# Revit family: Rohrschelle Titan HD, M12, Silikon
name_source: partatom
category: HLS-Bauteile
revit_build: Autodesk Revit 2017 (Build: 20190507_1515(x64)
units: mm (PartAtom-declared; Revit-internal decimal feet)

## family parameters
Arbeitsebenenbasiert = Ja
Beim Laden mit Abzugskörper schneiden = Nein
Bemaßung runder Anschluss = Durchmesser verwenden
Gemeinsam genutzt = Ja
Immer vertikal = Nein
Raumberechnungspunkt = Nein
Teiletyp = Normal

## types (30) — shared parameters
A = 22 mm  [stored 0.0721785 ft]
Anschluss = M12
Anschlußhöhe = 22 mm
Bauart = zweiteilig
Baustoffklasse = B2
Brandschutz = RAL GZ 656
DF1 = 29 mm  [stored 0.0951444 ft]
DS = 6 mm  [stored 0.019685 ft]
DVS = 13 mm
Dämmstärke = 6 mm  [stored 0.019685 ft]
Fabrikat = MEFA
Farbe Schalldämmeinlage = rot
Firma = MEFA Befestigungs- und Montagesysteme GmbH
HGA = 11 mm  [stored 0.0360892 ft]
Kurztext1 = Rohrschelle Titan HD 50x5,0
MB = 50 mm  [stored 0.164042 ft]
MD = 5 mm  [stored 0.0164042 ft]
Material = Stahl
Material Schalldämmeinlage = Silikon
Materialmaße = 50x5,0 mm
Materialname = S235
Mengeneinheit = St
Oberflaeche = galvanisch verzinkt
Schalldämmeinlage = Silikon
Verschluss = Schraubverschluss
Verschluss-Schraube = M12
Vorgabe-Ansicht = 1219 mm
max. Temperaturbeständigkeit = 250 °C
max. zul. Last horizontal = 0.00 kN
max. zul. Last vertikal = 0.00 kN
vpe = 1 St
zero-valued in all types: Nennweite DN Rohr, Stärke Material, max. Rohraußendurchmesser, min. Rohraußendurchmesser

## per-type parameters (varying)
| type | Achsabstand | Artikelnummer | B | Breite | D | D0 | DF2 | EAN | Gewicht | Gewicht pro Bauteil | H | Höhe | Kurztext2 | R | RM | Rohraußendurchmesser | Rohraußendurchmesser Zoll | S | max. Höhe | max. zul. Last |
| Titan HD, M12, Ø 64, Silikon | 125 mm | 0067500 | 154 mm | 154 mm | 64 mm  [stored 0.209974 ft] | 76 mm  [stored 0.249344 ft] | 19 mm  [stored 0.062336 ft] | 4250928402059 | 0.92 kg | 0.92 kg | 97 mm | 97 mm | 64 mm M12 Silikon | 38 mm  [stored 0.124672 ft] | 43 mm | 64 mm  [stored 0.209974 ft] | Zoll | 125 mm | 97 mm | 3.20 kN |
| Titan HD, M12, Ø 76, Silikon | 137 mm | 0067504 | 166 mm | 166 mm | 76 mm  [stored 0.249344 ft] | 88 mm  [stored 0.288714 ft] | 19 mm  [stored 0.062336 ft] | 4250928402066 | 1.01 kg | 1.01 kg | 109 mm | 109 mm | 76 mm M12 Silikon | 44 mm  [stored 0.144357 ft] | 49 mm | 76 mm  [stored 0.249344 ft] | 2 1/2 Zoll | 137 mm | 109 mm | 3.20 kN |
| Titan HD, M12, Ø 89, Silikon | 150 mm | 0067506 | 179 mm | 179 mm | 89 mm  [stored 0.291995 ft] | 101 mm | 19 mm  [stored 0.062336 ft] | 4250928402073 | 1.11 kg | 1.11 kg | 122 mm | 122 mm | 89 mm M12 Silikon | 51 mm | 56 mm | 89 mm  [stored 0.291995 ft] | 3 Zoll | 150 mm | 122 mm | 3.20 kN |
| Titan HD, M12, Ø108, Silikon | 170 mm | 0067512 | 199 mm | 199 mm | 108 mm | 120 mm | 20 mm  [stored 0.0656168 ft] | 4250928402080 | 1.25 kg | 1.25 kg | 141 mm | 141 mm | 108 mm M12 Silikon | 60 mm  [stored 0.19685 ft] | 65 mm | 108 mm | Zoll | 170 mm | 141 mm | 3.20 kN |
| Titan HD, M12, Ø110, Silikon | 170 mm | 0067539 | 201 mm | 199 mm | 110 mm | 122 mm | 20 mm  [stored 0.0656168 ft] | 4250928402080 | 1.25 kg | 1.25 kg | 143 mm | 141 mm | 108 mm M12 Silikon | 61 mm  [stored 0.200131 ft] | 66 mm | 108 mm | Zoll | 172 mm | 141 mm | 3.20 kN |
| Titan HD, M12, Ø133, Silikon | 195 mm | 0067601 | 224 mm | 224 mm | 133 mm | 145 mm | 20 mm  [stored 0.0656168 ft] | 4250928402134 | 1.44 kg | 1.44 kg | 166 mm | 166 mm | 133 mm M12 Silikon | 73 mm | 78 mm | 133 mm | Zoll | 195 mm | 166 mm | 3.20 kN |
| Titan HD, M12, Ø135, Silikon | 197 mm | 0067628 | 226 mm | 226 mm | 135 mm | 147 mm | 20 mm  [stored 0.0656168 ft] | 4250928402141 | 1.45 kg | 1.45 kg | 168 mm | 168 mm | 135 mm M12 Silikon | 74 mm | 79 mm | 135 mm | Zoll | 197 mm | 168 mm | 3.20 kN |
| Titan HD, M12, Ø140, Silikon | 202 mm | 0067636 | 231 mm | 231 mm | 140 mm | 152 mm | 20 mm  [stored 0.0656168 ft] | 4250928402158 | 1.49 kg | 1.49 kg | 173 mm | 173 mm | 140 mm M12 Silikon | 76 mm  [stored 0.249344 ft] | 81 mm  [stored 0.265748 ft] | 140 mm | 5 Zoll | 202 mm | 173 mm | 3.20 kN |
| Titan HD, M12, Ø160, Silikon | 222 mm | 0067687 | 251 mm | 251 mm | 160 mm | 172 mm | 20 mm  [stored 0.0656168 ft] | 4250928402172 | 1.64 kg | 1.64 kg | 193 mm | 193 mm | 160 mm M12 Silikon | 86 mm  [stored 0.282152 ft] | 91 mm  [stored 0.298556 ft] | 160 mm | Zoll | 222 mm | 193 mm | 3.20 kN |
| Titan HD, M12, Ø165, Silikon | 227 mm | 0067695 | 256 mm | 256 mm | 165 mm | 177 mm | 20 mm  [stored 0.0656168 ft] | 4250928402189 | 1.68 kg | 1.68 kg | 198 mm | 198 mm | 165 mm M12 Silikon | 89 mm  [stored 0.291995 ft] | 94 mm | 165 mm | 6 Zoll | 227 mm | 198 mm | 3.20 kN |
| Titan HD, M12, Ø168, Silikon | 230 mm | 0067717 | 259 mm | 259 mm | 168 mm | 180 mm | 20 mm  [stored 0.0656168 ft] | 4250928402196 | 1.70 kg | 1.70 kg | 201 mm | 201 mm | 168 mm M12 Silikon | 90 mm | 95 mm | 168 mm | Zoll | 230 mm | 201 mm | 3.20 kN |
| Titan HD, M12, Ø194, Silikon | 257 mm | 0067768 | 286 mm | 286 mm | 194 mm | 206 mm | 20 mm  [stored 0.0656168 ft] | 4250928402226 | 1.89 kg | 1.89 kg | 227 mm | 227 mm | 194 mm M12 Silikon | 103 mm | 108 mm | 194 mm | Zoll | 257 mm | 227 mm | 11.50 kN |
| Titan HD, M12, Ø200, Silikon | 263 mm | 0067784 | 292 mm | 292 mm | 200 mm | 212 mm | 20 mm  [stored 0.0656168 ft] | 4250928402233 | 1.94 kg | 1.94 kg | 233 mm | 233 mm | 200 mm M12 Silikon | 106 mm | 111 mm | 200 mm | Zoll | 263 mm | 233 mm | 11.50 kN |
| Titan HD, M12, Ø210, Silikon | 273 mm | 0067814 | 302 mm | 302 mm | 210 mm | 222 mm | 20 mm  [stored 0.0656168 ft] | 4250928402240 | 2.01 kg | 2.01 kg | 243 mm | 243 mm | 210 mm M12 Silikon | 111 mm | 116 mm | 210 mm | Zoll | 273 mm | 243 mm | 11.50 kN |
| Titan HD, M12, Ø219, Silikon | 282 mm | 0067822 | 311 mm | 311 mm | 219 mm | 231 mm | 20 mm  [stored 0.0656168 ft] | 4250928402257 | 2.08 kg | 2.08 kg | 252 mm | 252 mm | 219 mm M12 Silikon | 116 mm | 121 mm | 219 mm | 8 Zoll | 282 mm | 252 mm | 11.50 kN |
| Titan HD, M12, Ø267, Silikon | 330 mm | 0067881 | 359 mm | 359 mm | 267 mm | 279 mm | 20 mm  [stored 0.0656168 ft] | 4250928402288 | 2.44 kg | 2.44 kg | 300 mm | 300 mm | 267 mm M12 Silikon | 140 mm | 145 mm | 267 mm | Zoll | 330 mm | 300 mm | 11.50 kN |
| Titan HD, M12, Ø273, Silikon | 336 mm | 0067903 | 365 mm | 365 mm | 273 mm | 285 mm | 20 mm  [stored 0.0656168 ft] | 4250928402295 | 2.49 kg | 2.49 kg | 306 mm | 306 mm | 273 mm M12 Silikon | 143 mm | 148 mm | 273 mm | 10 Zoll | 336 mm | 306 mm | 11.50 kN |
| Titan HD, M12, Ø324, Silikon | 387 mm | 0067954 | 416 mm | 416 mm | 324 mm | 336 mm | 20 mm  [stored 0.0656168 ft] | 4250928402325 | 2.87 kg | 2.87 kg | 357 mm | 357 mm | 324 mm M12 Silikon | 168 mm | 173 mm | 324 mm | 12 Zoll | 387 mm | 357 mm | 11.50 kN |
| Titan HD, M12, Ø356, Silikon | 419 mm | 0067962 | 448 mm | 448 mm | 356 mm | 368 mm | 20 mm  [stored 0.0656168 ft] | 4250928402332 | 3.11 kg | 3.11 kg | 389 mm | 389 mm | 356 mm M12 Silikon | 184 mm | 189 mm | 356 mm | Zoll | 419 mm | 389 mm | 11.50 kN |
| Titan HD, M12, Ø368, Silikon | 431 mm | 0067989 | 460 mm | 460 mm | 368 mm | 380 mm | 20 mm  [stored 0.0656168 ft] | 4250928402349 | 3.20 kg | 3.20 kg | 401 mm | 401 mm | 368 mm M12 Silikon | 190 mm | 195 mm | 368 mm | Zoll | 431 mm | 401 mm | 11.50 kN |
| Titan HD, M12, Ø114, Silikon | 176 mm | 0067555 | 205 mm | 205 mm | 114 mm | 126 mm | 20 mm  [stored 0.0656168 ft] | 4250928402103 | 1.29 kg | 1.29 kg | 147 mm | 147 mm | 114 mm M12 Silikon | 63 mm  [stored 0.206693 ft] | 68 mm  [stored 0.223097 ft] | 114 mm | 4 Zoll | 176 mm | 147 mm | 3.20 kN |
| Titan HD, M12, Ø125, Silikon | 187 mm | 0067571 | 216 mm | 216 mm | 125 mm | 137 mm | 20 mm  [stored 0.0656168 ft] | 4250928402110 | 1.38 kg | 1.38 kg | 158 mm | 158 mm | 125 mm M12 Silikon | 69 mm | 74 mm | 125 mm | Zoll | 187 mm | 158 mm | 3.20 kN |
| Titan HD, M12, Ø127, Silikon | 189 mm | 0067598 | 218 mm | 218 mm | 127 mm | 139 mm | 20 mm  [stored 0.0656168 ft] | 4250928402127 | 1.39 kg | 1.39 kg | 160 mm | 160 mm | 127 mm M12 Silikon | 70 mm | 75 mm | 127 mm | Zoll | 189 mm | 160 mm | 3.20 kN |
| Titan HD, M12, Ø152, Silikon | 214 mm | 0067644 | 243 mm | 243 mm | 152 mm | 164 mm | 20 mm  [stored 0.0656168 ft] | 4250928402165 | 1.58 kg | 1.58 kg | 185 mm | 185 mm | 152 mm M12 Silikon | 82 mm  [stored 0.269029 ft] | 87 mm  [stored 0.285433 ft] | 152 mm | Zoll | 214 mm | 185 mm | 3.20 kN |
| Titan HD, M12, Ø177, Silikon | 242 mm | 0067733 | 268 mm | 271 mm | 177 mm | 189 mm | 20 mm  [stored 0.0656168 ft] | 4250928402219 | 1.79 kg | 1.79 kg | 210 mm | 213 mm | 180 mm M12 Silikon | 95 mm | 100 mm | 180 mm | Zoll | 239 mm | 213 mm | 11.50 kN |
| Titan HD, M12, Ø180, Silikon | 242 mm | 0067741 | 271 mm | 271 mm | 180 mm | 192 mm | 20 mm  [stored 0.0656168 ft] | 4250928402219 | 1.79 kg | 1.79 kg | 213 mm | 213 mm | 180 mm M12 Silikon | 96 mm | 101 mm | 180 mm | Zoll | 242 mm | 213 mm | 11.50 kN |
| Titan HD, M12, Ø225, Silikon | 288 mm | 0067849 | 317 mm | 317 mm | 225 mm | 237 mm | 20 mm  [stored 0.0656168 ft] | 4250928402264 | 2.13 kg | 2.13 kg | 258 mm | 258 mm | 225 mm M12 Silikon | 119 mm | 124 mm | 225 mm | Zoll | 288 mm | 258 mm | 11.50 kN |
| Titan HD, M12, Ø245, Silikon | 308 mm | 0067873 | 337 mm | 337 mm | 245 mm | 257 mm | 20 mm  [stored 0.0656168 ft] | 4250928402271 | 2.28 kg | 2.28 kg | 278 mm | 278 mm | 245 mm M12 Silikon | 129 mm | 134 mm | 245 mm | Zoll | 308 mm | 278 mm | 11.50 kN |
| Titan HD, M12, Ø280, Silikon | 343 mm | 0067911 | 372 mm | 372 mm | 280 mm | 292 mm | 20 mm  [stored 0.0656168 ft] | 4250928402301 | 2.54 kg | 2.54 kg | 313 mm | 313 mm | 280 mm M12 Silikon | 146 mm | 151 mm | 280 mm | Zoll | 343 mm | 313 mm | 11.50 kN |
| Titan HD, M12, Ø298, Silikon | 361 mm | 0067938 | 390 mm | 390 mm | 298 mm | 310 mm | 20 mm  [stored 0.0656168 ft] | 4250928402318 | 2.67 kg | 2.67 kg | 331 mm | 331 mm | 298 mm M12 Silikon | 155 mm | 160 mm | 298 mm | Zoll | 361 mm | 331 mm | 11.50 kN |

note: [stored X ft] marks values corroborated as IEEE doubles in the binary element streams (Revit-internal decimal feet)

## geometry (parser evidence)
native form markers: Sweep x4
no freeform markers — native parametric forms only
